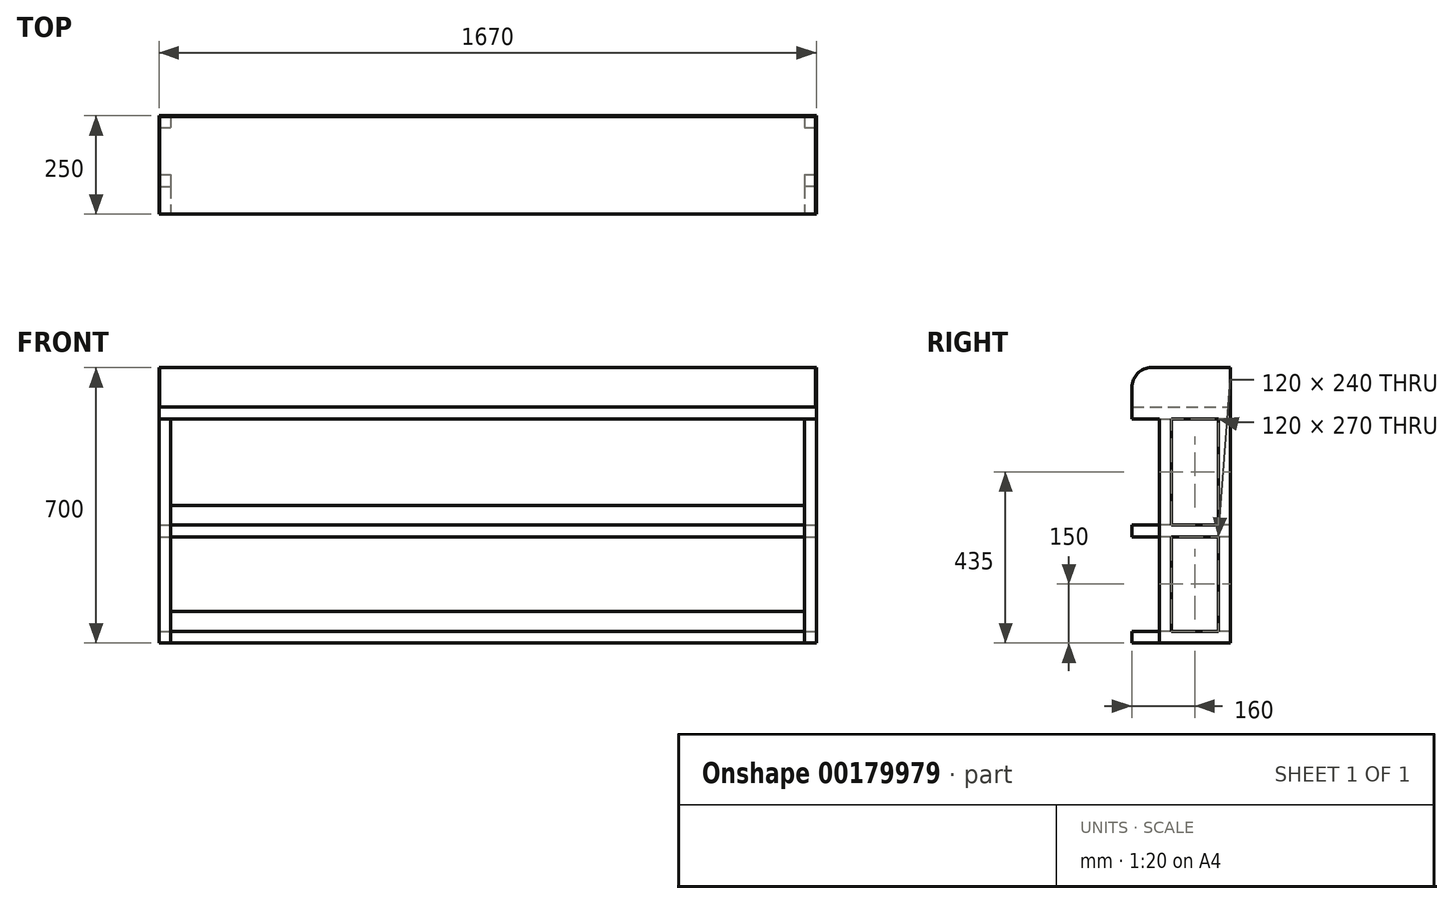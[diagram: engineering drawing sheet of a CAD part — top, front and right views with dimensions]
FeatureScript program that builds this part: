
annotation { "Feature Type Name" : "Feature", "Feature Type Description" : "" }
export const myFeature = defineFeature(function(context is Context, id is Id, definition is map)
    precondition{}
    {
        {
            var Q0;
            Q0=qCreatedBy(makeId("Top.planeOp"),FACE);
            var sketch = newSketch(context, id + "F0", { "sketchPlane" : qUnion([Q0])});
            skLineSegment(sketch, "E0.bottom", {"start": v(835, 125) * mm, "end": v(-835, 125) * mm});
            skLineSegment(sketch, "E0.top", {"start": v(835, -125) * mm, "end": v(-835, -125) * mm});
            skLineSegment(sketch, "E0.left", {"start": v(835, 125) * mm, "end": v(835, -125) * mm});
            skLineSegment(sketch, "E0.right", {"start": v(-835, 125) * mm, "end": v(-835, -125) * mm});
            skPoint(sketch, "E0.middle", {"position": v(0, 0) * mm});
            skSolve(sketch);
        }
        {
            var Q0;
            Q0 = qSketchRegion(id + "F0", true);
            extrude(context, id + "F1", {"entities" : qUnion([Q0]), "depth" : 30 * mm});
        }
        {
            var Q0;
            Q0=makeQuery(id+"F1.opExtrude","CAP_FACE",FACE,{"disambiguationData":[OSD([sQuery(id+"F0.wireOp",EDGE,"E0.bottom"),sQuery(id+"F0.wireOp",EDGE,"E0.top"),sQuery(id+"F0.wireOp",EDGE,"E0.left"),sQuery(id+"F0.wireOp",EDGE,"E0.right")])],"isStart":true});
            var sketch = newSketch(context, id + "F2", { "sketchPlane" : qUnion([Q0])});
            skLineSegment(sketch, "E1.bottom", {"start": v(-835, 55) * mm, "end": v(-805, 55) * mm});
            skLineSegment(sketch, "E1.top", {"start": v(-835, 25) * mm, "end": v(-805, 25) * mm});
            skLineSegment(sketch, "E1.left", {"start": v(-835, 55) * mm, "end": v(-835, 25) * mm});
            skLineSegment(sketch, "E1.right", {"start": v(-805, 55) * mm, "end": v(-805, 25) * mm});
            skLineSegment(sketch, "E2.bottom", {"start": v(835, 55) * mm, "end": v(805, 55) * mm});
            skLineSegment(sketch, "E2.top", {"start": v(835, 25) * mm, "end": v(805, 25) * mm});
            skLineSegment(sketch, "E2.left", {"start": v(835, 55) * mm, "end": v(835, 25) * mm});
            skLineSegment(sketch, "E2.right", {"start": v(805, 55) * mm, "end": v(805, 25) * mm});
            skLineSegment(sketch, "E3.bottom", {"start": v(835, -125) * mm, "end": v(805, -125) * mm});
            skLineSegment(sketch, "E3.top", {"start": v(835, -95) * mm, "end": v(805, -95) * mm});
            skLineSegment(sketch, "E3.left", {"start": v(835, -125) * mm, "end": v(835, -95) * mm});
            skLineSegment(sketch, "E3.right", {"start": v(805, -125) * mm, "end": v(805, -95) * mm});
            skLineSegment(sketch, "E4.bottom", {"start": v(-835, -125) * mm, "end": v(-805, -125) * mm});
            skLineSegment(sketch, "E4.top", {"start": v(-835, -95) * mm, "end": v(-805, -95) * mm});
            skLineSegment(sketch, "E4.left", {"start": v(-835, -125) * mm, "end": v(-835, -95) * mm});
            skLineSegment(sketch, "E4.right", {"start": v(-805, -125) * mm, "end": v(-805, -95) * mm});
            skSolve(sketch);
        }
        {
            var Q0;
            Q0 = qSketchRegion(id + "F2", true);
            extrude(context, id + "F3", {"entities" : qUnion([Q0]), "operationType" : NewBodyOperationType.ADD, "depth" : 570 * mm, "offsetDistance" : 25 * mm});
        }
        {
            var Q0;
            Q0=qCreatedBy(makeId("Right.planeOp"),FACE);
            var sketch = newSketch(context, id + "F4", { "sketchPlane" : qUnion([Q0])});
            skLineSegment(sketch, "E5.bottom", {"start": v(-125, -270) * mm, "end": v(125, -270) * mm});
            skLineSegment(sketch, "E5.top", {"start": v(-125, -300) * mm, "end": v(125, -300) * mm});
            skLineSegment(sketch, "E5.left", {"start": v(-125, -270) * mm, "end": v(-125, -300) * mm});
            skLineSegment(sketch, "E5.right", {"start": v(125, -270) * mm, "end": v(125, -300) * mm});
            skLineSegment(sketch, "E6.bottom", {"start": v(-125, -540) * mm, "end": v(125, -540) * mm});
            skLineSegment(sketch, "E6.top", {"start": v(-125, -570) * mm, "end": v(125, -570) * mm});
            skLineSegment(sketch, "E6.left", {"start": v(-125, -540) * mm, "end": v(-125, -570) * mm});
            skLineSegment(sketch, "E6.right", {"start": v(125, -540) * mm, "end": v(125, -570) * mm});
            skSolve(sketch);
        }
        {
            var Q0;
            Q0 = qSketchRegion(id + "F4", true);
            var Q1;
            Q1=makeQuery(id+"F3.opExtrude","SWEPT_FACE",FACE,{"disambiguationData":[OSD([sQuery(id+"F2.wireOp",EDGE,"E3.right")])]});
            var Q2;
            Q2=makeQuery(id+"F3.opExtrude","SWEPT_FACE",FACE,{"disambiguationData":[OSD([sQuery(id+"F2.wireOp",EDGE,"E4.right")])]});
            extrude(context, id + "F5", {"entities" : qUnion([Q0]), "operationType" : NewBodyOperationType.ADD, "endBound" : BoundingType.UP_TO_SURFACE, "endBoundEntityFace" : qUnion([Q1]), "depth" : 25 * mm, "hasSecondDirection" : true, "secondDirectionBound" : SecondDirectionBoundingType.UP_TO_SURFACE, "secondDirectionOppositeDirection" : true, "secondDirectionBoundEntityFace" : qUnion([Q2]), "secondDirectionDepth" : 25 * mm, "offsetDistance" : 25 * mm});
        }
        {
            var Q0;
            Q0=makeQuery(id+"F1.opExtrude","CAP_FACE",FACE,{"disambiguationData":[OSD([sQuery(id+"F0.wireOp",EDGE,"E0.bottom"),sQuery(id+"F0.wireOp",EDGE,"E0.top"),sQuery(id+"F0.wireOp",EDGE,"E0.left"),sQuery(id+"F0.wireOp",EDGE,"E0.right")])],"isStart":false});
            var sketch = newSketch(context, id + "F6", { "sketchPlane" : qUnion([Q0])});
            skLineSegment(sketch, "E7", {"start": v(-835, -125) * mm, "end": v(-835, 125) * mm});
            skLineSegment(sketch, "E8", {"start": v(-835, 125) * mm, "end": v(835, 125) * mm});
            skLineSegment(sketch, "E9", {"start": v(835, 125) * mm, "end": v(835, -125) * mm});
            skLineSegment(sketch, "E10", {"start": v(835, -125) * mm, "end": v(833, -125) * mm});
            skLineSegment(sketch, "E11", {"start": v(833, -125) * mm, "end": v(833, 123) * mm});
            skLineSegment(sketch, "E12", {"start": v(833, 123) * mm, "end": v(-833, 123) * mm});
            skLineSegment(sketch, "E13", {"start": v(-833, 123) * mm, "end": v(-833, -125) * mm});
            skLineSegment(sketch, "E14", {"start": v(-833, -125) * mm, "end": v(-835, -125) * mm});
            skSolve(sketch);
        }
        {
            var Q0;
            Q0 = qSketchRegion(id + "F6", true);
            extrude(context, id + "F7", {"entities" : qUnion([Q0]), "operationType" : NewBodyOperationType.ADD, "depth" : 100 * mm, "offsetDistance" : 25 * mm});
        }
        {
            var Q0;
            Q0=makeQuery(id+"F7.opExtrude","CAP_EDGE",EDGE,{"disambiguationData":[OSD([sQuery(id+"F6.wireOp",EDGE,"E14")])],"isStart":false});
            var Q1;
            Q1=makeQuery(id+"F7.opExtrude","CAP_EDGE",EDGE,{"disambiguationData":[OSD([sQuery(id+"F6.wireOp",EDGE,"E10")])],"isStart":false});
            fillet(context, id + "F8", {"entities" : qUnion([Q0, Q1]), "radius" : 50 * mm, "tangentPropagation" : true, "allowEdgeOverflow" : false});
        }
        {
            var Q0;
            Q0=makeQuery(id+"F5.opExtrude","SWEPT_FACE",FACE,{"disambiguationData":[OSD([sQuery(id+"F4.wireOp",EDGE,"E5.bottom")])]});
            var sketch = newSketch(context, id + "F9", { "sketchPlane" : qUnion([Q0])});
            skLineSegment(sketch, "E15.bottom", {"start": v(-805, 125) * mm, "end": v(805, 125) * mm});
            skLineSegment(sketch, "E15.top", {"start": v(-805, 123) * mm, "end": v(805, 123) * mm});
            skLineSegment(sketch, "E15.left", {"start": v(-805, 125) * mm, "end": v(-805, 123) * mm});
            skLineSegment(sketch, "E15.right", {"start": v(805, 125) * mm, "end": v(805, 123) * mm});
            skSolve(sketch);
        }
        {
            var Q0;
            Q0 = qSketchRegion(id + "F9", true);
            extrude(context, id + "F10", {"entities" : qUnion([Q0]), "operationType" : NewBodyOperationType.ADD, "depth" : 50 * mm, "offsetDistance" : 25 * mm});
        }
        {
            var Q0;
            Q0=makeQuery(id+"F5.opExtrude","SWEPT_FACE",FACE,{"disambiguationData":[OSD([sQuery(id+"F4.wireOp",EDGE,"E6.bottom")])]});
            var sketch = newSketch(context, id + "F11", { "sketchPlane" : qUnion([Q0])});
            skLineSegment(sketch, "E16.bottom", {"start": v(805, 125) * mm, "end": v(-805, 125) * mm});
            skLineSegment(sketch, "E16.top", {"start": v(805, 123) * mm, "end": v(-805, 123) * mm});
            skLineSegment(sketch, "E16.left", {"start": v(805, 125) * mm, "end": v(805, 123) * mm});
            skLineSegment(sketch, "E16.right", {"start": v(-805, 125) * mm, "end": v(-805, 123) * mm});
            skSolve(sketch);
        }
        {
            var Q0;
            Q0 = qSketchRegion(id + "F11", true);
            extrude(context, id + "F12", {"entities" : qUnion([Q0]), "operationType" : NewBodyOperationType.ADD, "depth" : 50 * mm, "offsetDistance" : 25 * mm});
        }
        {
            var Q0;
            Q0=qCreatedBy(makeId("Front.planeOp"),FACE);
            var sketch = newSketch(context, id + "F13", { "sketchPlane" : qUnion([Q0])});
            skLineSegment(sketch, "E17.bottom", {"start": v(835, -270) * mm, "end": v(805, -270) * mm});
            skLineSegment(sketch, "E17.top", {"start": v(835, -300) * mm, "end": v(805, -300) * mm});
            skLineSegment(sketch, "E17.left", {"start": v(835, -270) * mm, "end": v(835, -300) * mm});
            skLineSegment(sketch, "E17.right", {"start": v(805, -270) * mm, "end": v(805, -300) * mm});
            skLineSegment(sketch, "E18.bottom", {"start": v(835, -540) * mm, "end": v(805, -540) * mm});
            skLineSegment(sketch, "E18.top", {"start": v(835, -570) * mm, "end": v(805, -570) * mm});
            skLineSegment(sketch, "E18.left", {"start": v(835, -540) * mm, "end": v(835, -570) * mm});
            skLineSegment(sketch, "E18.right", {"start": v(805, -540) * mm, "end": v(805, -570) * mm});
            skLineSegment(sketch, "E19.bottom", {"start": v(-835, -540) * mm, "end": v(-805, -540) * mm});
            skLineSegment(sketch, "E19.top", {"start": v(-835, -570) * mm, "end": v(-805, -570) * mm});
            skLineSegment(sketch, "E19.left", {"start": v(-835, -540) * mm, "end": v(-835, -570) * mm});
            skLineSegment(sketch, "E19.right", {"start": v(-805, -540) * mm, "end": v(-805, -570) * mm});
            skPoint(sketch, "E20.oppositeSnap0", {"position": v(-805, -555) * mm});
            skLineSegment(sketch, "E20.bottom", {"start": v(-835, -270) * mm, "end": v(-805, -270) * mm});
            skLineSegment(sketch, "E20.top", {"start": v(-835, -300) * mm, "end": v(-805, -300) * mm});
            skLineSegment(sketch, "E20.left", {"start": v(-835, -270) * mm, "end": v(-835, -300) * mm});
            skLineSegment(sketch, "E20.right", {"start": v(-805, -270) * mm, "end": v(-805, -300) * mm});
            skSolve(sketch);
        }
        {
            var Q0;
            Q0 = qSketchRegion(id + "F13", true);
            extrude(context, id + "F14", {"entities" : qUnion([Q0]), "operationType" : NewBodyOperationType.ADD, "endBound" : BoundingType.UP_TO_NEXT, "depth" : 25 * mm, "offsetDistance" : 25 * mm, "hasSecondDirection" : true, "secondDirectionBound" : SecondDirectionBoundingType.UP_TO_NEXT, "secondDirectionOppositeDirection" : true, "secondDirectionDepth" : 25 * mm});
        }
    });
